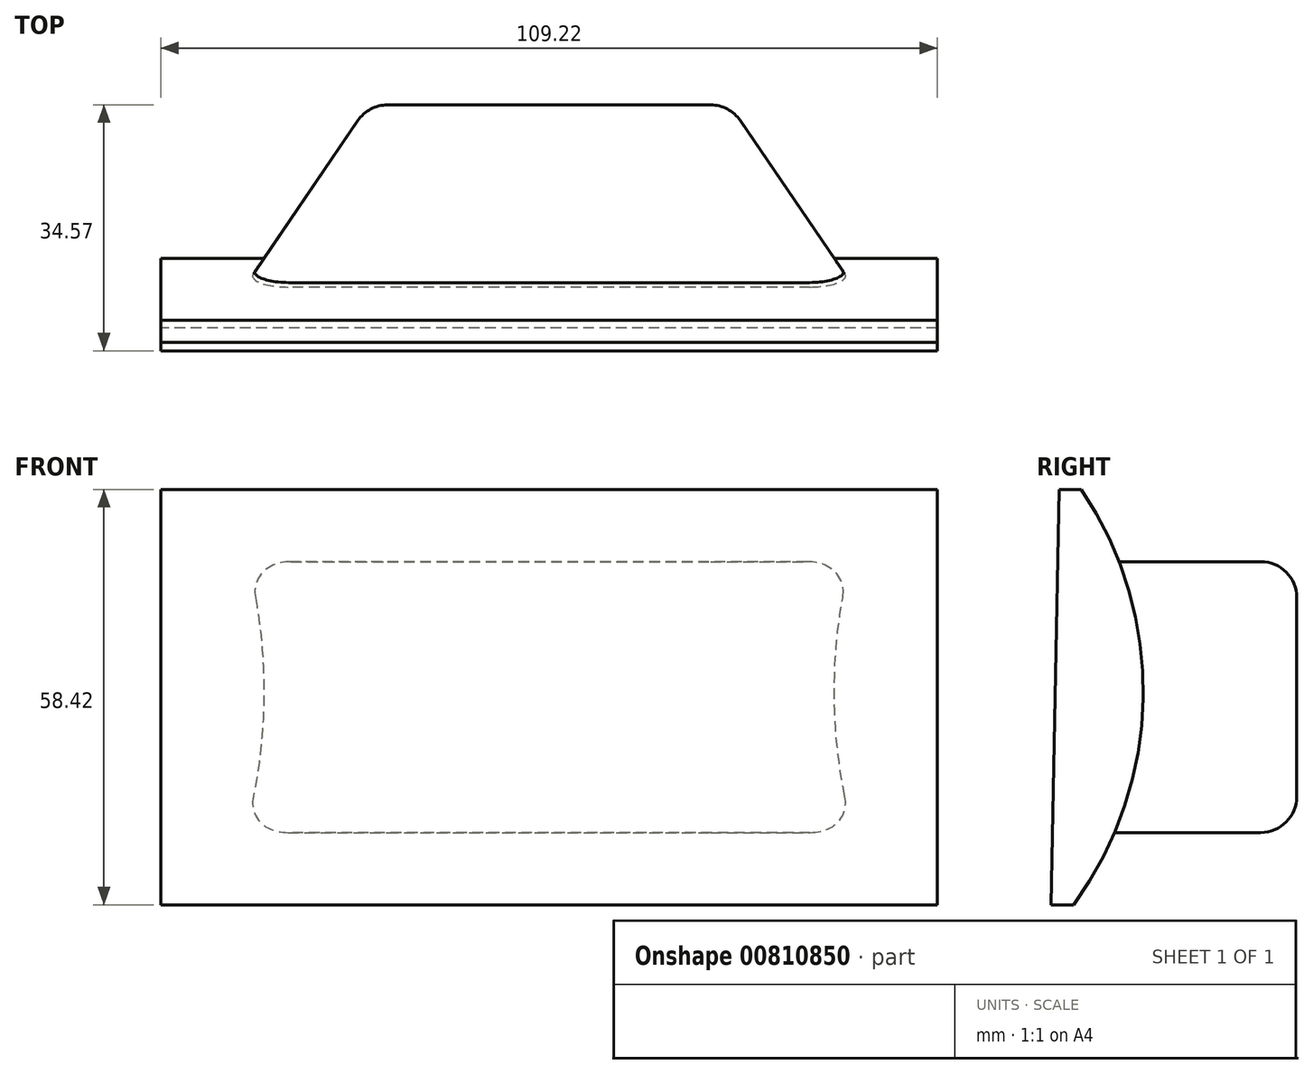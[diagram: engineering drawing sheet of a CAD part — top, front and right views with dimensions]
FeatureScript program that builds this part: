
annotation { "Feature Type Name" : "Feature", "Feature Type Description" : "" }
export const myFeature = defineFeature(function(context is Context, id is Id, definition is map)
    precondition{}
    {
        {
            var Q0;
            Q0=qCreatedBy(makeId("Right.planeOp"),FACE);
            cPlane(context, id + "F0", {"entities" : qUnion([Q0]), "cplaneType" : CPlaneType.OFFSET, "offset" : 41.9 * mm, "width" : 152.4 * mm, "height" : 152.4 * mm});
        }
        {
            var Q0;
            Q0=qCreatedBy(makeId("Top.planeOp"),FACE);
            var sketch = newSketch(context, id + "F1", { "sketchPlane" : qUnion([Q0])});
            skLineSegment(sketch, "E0", {"start": v(-44.45, 0) * mm, "end": v(-25.4, 27.94) * mm});
            skLineSegment(sketch, "E1", {"start": v(-25.4, 27.94) * mm, "end": v(25.4, 27.94) * mm});
            skLineSegment(sketch, "E2", {"start": v(25.4, 27.94) * mm, "end": v(44.45, 0) * mm});
            skLineSegment(sketch, "E3", {"start": v(44.45, 0) * mm, "end": v(-44.45, 0) * mm});
            skPoint(sketch, "E4", {"position": v(0, 27.94) * mm});
            skLineSegment(sketch, "E5.0", {"start": v(-23.39, 24.13) * mm, "end": v(23.39, 24.13) * mm});
            skLineSegment(sketch, "E5.1", {"start": v(-37.24, 3.81) * mm, "end": v(-23.39, 24.13) * mm});
            skLineSegment(sketch, "E5.2", {"start": v(37.24, 3.81) * mm, "end": v(-37.24, 3.81) * mm});
            skLineSegment(sketch, "E5.3", {"start": v(23.39, 24.13) * mm, "end": v(37.24, 3.81) * mm});
            skSolve(sketch);
        }
        {
            var Q0;
            Q0=makeQuery(id+"F1.imprint","IMPRINT",FACE,{"disambiguationData":[TD([[makeQuery(id+"F1.imprint","IMPRINT",EDGE,{"derivedFrom":sQuery(id+"F1.wireOp",EDGE,"E0")}),-1.0]])]});
            var Q1;
            Q1=makeQuery(id+"F1.imprint","IMPRINT",FACE,{"disambiguationData":[TD([[makeQuery(id+"F1.imprint","IMPRINT",EDGE,{"derivedFrom":sQuery(id+"F1.wireOp",EDGE,"E5.0")}),-1.0]])]});
            extrude(context, id + "F2", {"entities" : qUnion([Q0, Q1]), "depth" : 38.1 * mm, "offsetDistance" : 25.4 * mm});
        }
        {
            var Q0;
            Q0=qCreatedBy(id+"F0.planeOp",FACE);
            var sketch = newSketch(context, id + "F3", { "sketchPlane" : qUnion([Q0])});
            skLineSegment(sketch, "E6", {"start": v(6.35, 0) * mm, "end": v(6.35, 38.66) * mm});
            skCircle(sketch, "E7", {"center": v(-44.45, 19.82) * mm, "radius": 50.8 * mm});
            skPoint(sketch, "E8", {"position": v(6.35, 19.33) * mm});
            skCircle(sketch, "E9.0", {"center": v(-44.45, 19.82) * mm, "radius": 48.26 * mm});
            skLineSegment(sketch, "E10", {"start": v(-2.36, 48.26) * mm, "end": v(-5.46, 48.26) * mm});
            skLineSegment(sketch, "E11", {"start": v(-3.44, -10.16) * mm, "end": v(-6.63, -10.16) * mm});
            skLineSegment(sketch, "E12", {"start": v(-5.46, 48.26) * mm, "end": v(-6.63, -10.16) * mm});
            skSolve(sketch);
        }
        {
            var Q0;
            {var subQ0=sQuery(id+"F3.wireOp",EDGE,"E10");Q0=makeQuery(id+"F3.imprint","IMPRINT",FACE,{"disambiguationData":[TD([[makeQuery(id+"F3.imprint","IMPRINT",EDGE,{"derivedFrom":subQ0}),1.0]])]});}
            var Q1;
            {var subQ0=sQuery(id+"F3.wireOp",EDGE,"E12");Q1=makeQuery(id+"F3.imprint","IMPRINT",FACE,{"disambiguationData":[TD([[makeQuery(id+"F3.imprint","IMPRINT",EDGE,{"derivedFrom":subQ0}),1.0]])]});}
            extrude(context, id + "F4", {"entities" : qUnion([Q0, Q1]), "operationType" : NewBodyOperationType.ADD, "depth" : 12.7 * mm, "offsetDistance" : 25.4 * mm, "hasSecondDirection" : true, "secondDirectionOppositeDirection" : true, "secondDirectionDepth" : 96.52 * mm});
        }
        {
            var Q0;
            Q0=makeQuery(id+"F2.opExtrude","SWEPT_EDGE",EDGE,{"disambiguationData":[OSD([sQuery(id+"F1.wireOp",EDGE,"E1"),sQuery(id+"F1.wireOp",EDGE,"E2")])]});
            var Q1;
            Q1=makeQuery(id+"F2.opExtrude","SWEPT_EDGE",EDGE,{"disambiguationData":[OSD([sQuery(id+"F1.wireOp",EDGE,"E0"),sQuery(id+"F1.wireOp",EDGE,"E1")])]});
            fillet(context, id + "F5", {"entities" : qUnion([Q0, Q1]), "radius" : 5.08 * mm, "tangentPropagation" : true, "allowEdgeOverflow" : false});
        }
        {
            var Q0;
            Q0=qCreatedBy(makeId("Top.planeOp"),FACE);
            cPlane(context, id + "F6", {"entities" : qUnion([Q0]), "cplaneType" : CPlaneType.OFFSET, "offset" : 38.1 * mm, "width" : 152.4 * mm, "height" : 152.4 * mm});
        }
        {
            var Q0;
            Q0=makeQuery(id+"F2.opExtrude","CAP_EDGE",EDGE,{"disambiguationData":[OSD([sQuery(id+"F1.wireOp",EDGE,"E2")])],"isStart":true});
            fillet(context, id + "F7", {"entities" : qUnion([Q0]), "radius" : 5.08 * mm, "tangentPropagation" : true, "allowEdgeOverflow" : false});
        }
        {
            var Q0;
            Q0=makeQuery(id+"F2.opExtrude","CAP_EDGE",EDGE,{"disambiguationData":[OSD([sQuery(id+"F1.wireOp",EDGE,"E0")])],"isStart":false});
            fillet(context, id + "F8", {"entities" : qUnion([Q0]), "radius" : 5.08 * mm, "tangentPropagation" : true, "allowEdgeOverflow" : false});
        }
    });
